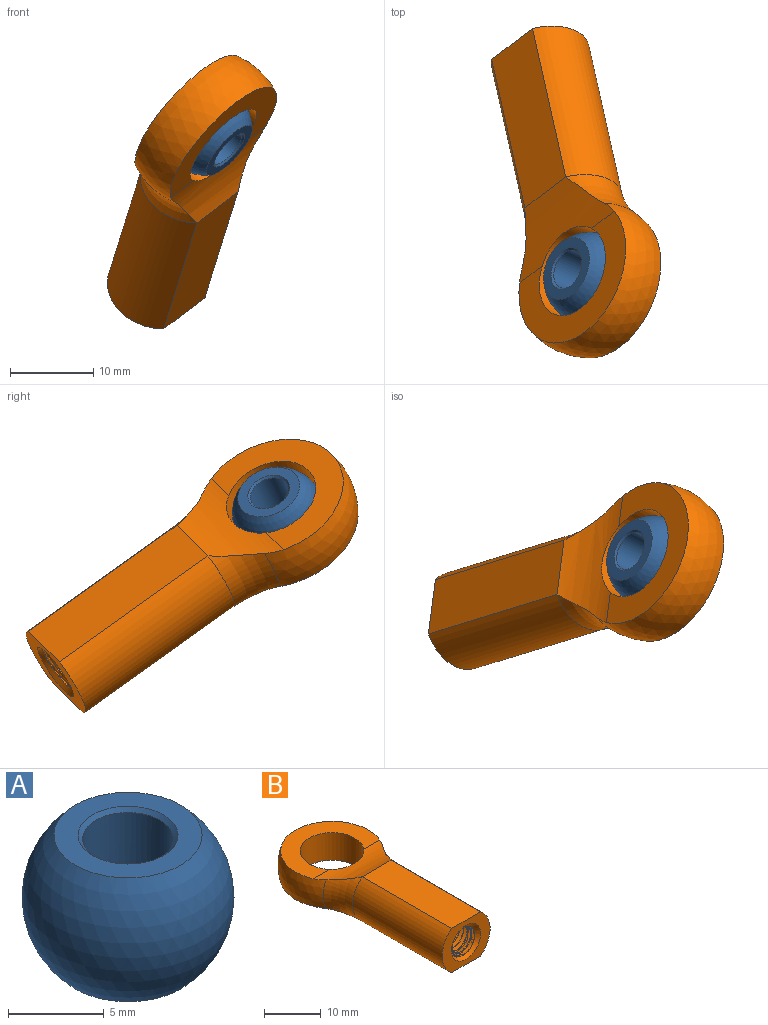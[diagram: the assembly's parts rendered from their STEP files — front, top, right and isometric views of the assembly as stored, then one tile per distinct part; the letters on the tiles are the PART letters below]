
ASSEMBLY  parts=2 mates=1
PART A: 6 faces, bbox 11.1x11.1x7.9 mm
  f0: cone r=2.62mm half-angle=45deg, axis (0,0,1), area 5.3mm2, adj f2,f4
  f1: cone r=2.62mm half-angle=45deg, axis (0,0,-1), area 5.3mm2, adj f2,f5
  f2: cylinder r=2.38mm len=7.46mm, axis (0,0,1), area 111.6mm2, adj f0,f1
  f3: sphere r=5.55mm, area 276.8mm2, adj f4,f5
  f4: plane 7.76x7.76mm, normal (0,0,1), area 25.7mm2, adj f0,f3
  f5: plane 7.76x7.76mm, normal (0,0,-1), area 25.7mm2, adj f1,f3
PART B: 19 faces, bbox 19.4x43.2x15.4 mm
  f0: cylinder r=5.61mm len=11.21mm, axis (0,0,1), area 209.3mm2, adj f15,f16,f17,f18
  f1: sphere r=9.53mm, area 253.6mm2, adj f2,f6,f15,f16,f17,f18
  f2: torus R=15.48mm, axis (0,-1,0), area 51mm2, adj f1,f8,f17,f18
  f3: cylinder r=3.17mm len=17.01mm, axis (0,-1,0), area 42.4mm2, adj f4,f9,f10,f12
  f4: cone r=3.63mm half-angle=45deg, axis (0,-1,0), area 21.4mm2, adj f3,f7,f10,f11,f12
  f5: cylinder r=5.96mm len=22.24mm, axis (0,1,0), area 245.4mm2, adj f6,f7,f13,f14
  f6: torus R=15.48mm, axis (0,-1,0), area 51mm2, adj f1,f5,f17,f18
  f7: plane 11.91x9.53mm, normal (0,-1,0), area 58.5mm2, adj f4,f5,f8,f13,f14
  f8: cylinder r=5.96mm len=22.24mm, axis (0,1,0), area 245.4mm2, adj f2,f7,f13,f14
  f9: plane 6.16x6.14mm, normal (0,-1,0), area 26.2mm2, adj f3,f10,f11,f12
  f10: bspline ~17.46x6.35mm, area 227.2mm2, adj f3,f4,f9,f11
  f11: cylinder r=2.59mm len=16.42mm, axis (0,1,0), area 33.2mm2, adj f4,f9,f10,f12
  f12: bspline ~17.8x6.35mm, area 226.8mm2, adj f3,f4,f9,f11
  f13: plane 22.24x7.15mm, normal (0,0,1), area 159.1mm2, adj f5,f7,f8,f17
  f14: plane 22.24x7.15mm, normal (0,0,-1), area 159.1mm2, adj f5,f7,f8,f18
  f15: plane 18.1x12.63mm, normal (0,0,1), area 105.2mm2, adj f0,f1,f17
  f16: plane 18.1x12.63mm, normal (0,0,-1), area 105.2mm2, adj f0,f1,f18
  f17: cylinder r=16.67mm len=16.62mm, axis (-1,0,0), area 80.4mm2, adj f0,f1,f2,f6,f13,f15
  f18: cylinder r=16.67mm len=16.62mm, axis (1,0,0), area 80.4mm2, adj f0,f1,f2,f6,f14,f16
PLACE A rot(axis=(-0.21,0.94,-0.26),139.6deg) t=(73.13,-177.55,34.42)mm
PLACE B rot(axis=(0.35,-0.25,-0.9),157.3deg) t=(67.45,-152.12,16.29)mm
MATE ball A.f0 <-> B.f0  axis (0.71,-0.3,-0.64) through (70.29,-164.84,25.36)mm
